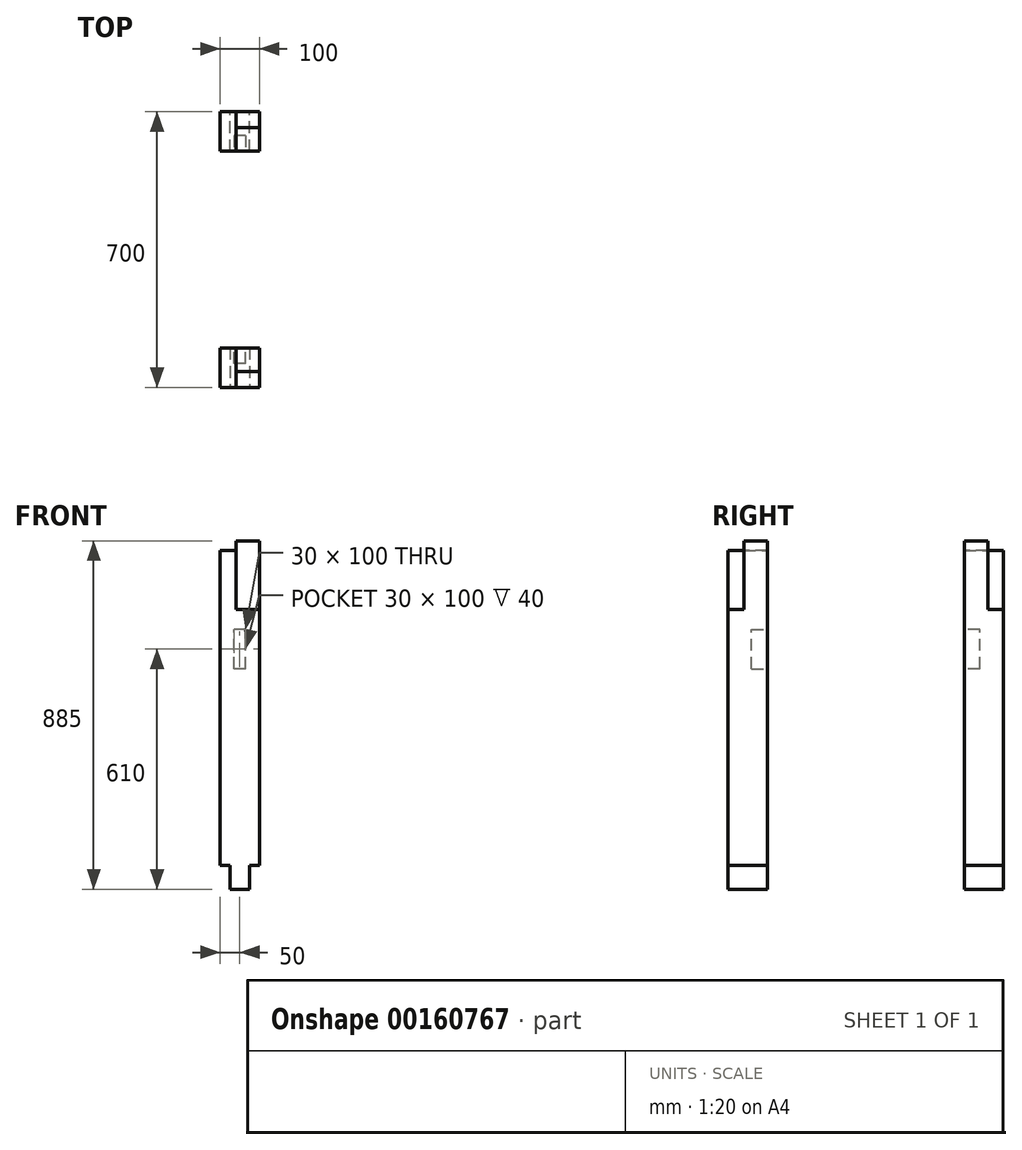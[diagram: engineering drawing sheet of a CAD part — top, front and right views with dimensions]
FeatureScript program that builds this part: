
annotation { "Feature Type Name" : "Feature", "Feature Type Description" : "" }
export const myFeature = defineFeature(function(context is Context, id is Id, definition is map)
    precondition{}
    {
        {
            assignVariable(context, id + "F0", {"name" : "L", "anyValue" : 800 * mm});
        }
        {
            assignVariable(context, id + "F1", {"name" : "t_Feder", "anyValue" : 60 * mm});
        }
        {
            assignVariable(context, id + "F2", {"name" : "t_Tasche", "anyValue" : 40 * mm});
        }
        {
            var Q0;
            Q0=qCreatedBy(makeId("Top.planeOp"),FACE);
            var sketch = newSketch(context, id + "F3", { "sketchPlane" : qUnion([Q0])});
            skLineSegment(sketch, "E0.bottom", {"start": v(50, -50) * mm, "end": v(-50, -50) * mm});
            skLineSegment(sketch, "E0.top", {"start": v(50, 50) * mm, "end": v(-50, 50) * mm});
            skLineSegment(sketch, "E0.left", {"start": v(50, -50) * mm, "end": v(50, 50) * mm});
            skLineSegment(sketch, "E0.right", {"start": v(-50, -50) * mm, "end": v(-50, 50) * mm});
            skPoint(sketch, "E0.middle", {"position": v(0, 0) * mm});
            skSolve(sketch);
        }
        {
            var Q0;
            Q0 = qSketchRegion(id + "F3", true);
            extrude(context, id + "F4", {"entities" : qUnion([Q0]), "depth" : getVariable(context, 'L')});
        }
        {
            var Q0;
            Q0=makeQuery(id+"F4.opExtrude","CAP_FACE",FACE,{"disambiguationData":[OSD([sQuery(id+"F3.wireOp",EDGE,"E0.bottom"),sQuery(id+"F3.wireOp",EDGE,"E0.top"),sQuery(id+"F3.wireOp",EDGE,"E0.left"),sQuery(id+"F3.wireOp",EDGE,"E0.right")])],"isStart":true});
            var sketch = newSketch(context, id + "F5", { "sketchPlane" : qUnion([Q0])});
            skLineSegment(sketch, "E1.bottom", {"start": v(-25, 50) * mm, "end": v(25, 50) * mm});
            skLineSegment(sketch, "E1.top", {"start": v(-25, -50) * mm, "end": v(25, -50) * mm});
            skLineSegment(sketch, "E1.left", {"start": v(-25, 50) * mm, "end": v(-25, -50) * mm});
            skLineSegment(sketch, "E1.right", {"start": v(25, 50) * mm, "end": v(25, -50) * mm});
            skPoint(sketch, "E1.middle", {"position": v(0, 0) * mm});
            skSolve(sketch);
        }
        {
            var Q0;
            Q0 = qSketchRegion(id + "F5", true);
            extrude(context, id + "F6", {"entities" : qUnion([Q0]), "operationType" : NewBodyOperationType.ADD, "depth" : getVariable(context, 't_Feder')});
        }
        {
            var Q0;
            Q0=makeQuery(id+"F6.boolean.opBoolean","MERGE",FACE,{"derivedFrom":[makeQuery(id+"F4.opExtrude","SWEPT_FACE",FACE,{"disambiguationData":[OSD([sQuery(id+"F3.wireOp",EDGE,"E0.bottom")])]}),makeQuery(id+"F6.opExtrude","SWEPT_FACE",FACE,{"disambiguationData":[OSD([sQuery(id+"F5.wireOp",EDGE,"E1.bottom")])]})]});
            var sketch = newSketch(context, id + "F7", { "sketchPlane" : qUnion([Q0])});
            skLineSegment(sketch, "E2.bottom", {"start": v(50, 600) * mm, "end": v(-50, 600) * mm, "construction": true});
            skLineSegment(sketch, "E2.top", {"start": v(50, 500) * mm, "end": v(-50, 500) * mm, "construction": true});
            skLineSegment(sketch, "E2.left", {"start": v(50, 600) * mm, "end": v(50, 500) * mm, "construction": true});
            skLineSegment(sketch, "E2.right", {"start": v(-50, 600) * mm, "end": v(-50, 500) * mm, "construction": true});
            skPoint(sketch, "E2.middle", {"position": v(0, 550) * mm});
            skLineSegment(sketch, "E3", {"start": v(0, 800) * mm, "end": v(0, 550) * mm, "construction": true});
            skLineSegment(sketch, "E4.bottom", {"start": v(15, 500) * mm, "end": v(-15, 500) * mm});
            skLineSegment(sketch, "E4.top", {"start": v(15, 600) * mm, "end": v(-15, 600) * mm});
            skLineSegment(sketch, "E4.left", {"start": v(15, 500) * mm, "end": v(15, 600) * mm});
            skLineSegment(sketch, "E4.right", {"start": v(-15, 500) * mm, "end": v(-15, 600) * mm});
            skSolve(sketch);
        }
        {
            var Q0;
            Q0 = qSketchRegion(id + "F7", true);
            extrude(context, id + "F8", {"entities" : qUnion([Q0]), "operationType" : NewBodyOperationType.REMOVE, "oppositeDirection" : true, "depth" : getVariable(context, 't_Tasche')});
        }
        {
            var Q0;
            Q0=makeQuery(id+"F6.boolean.opBoolean","MERGE",FACE,{"derivedFrom":[makeQuery(id+"F4.opExtrude","SWEPT_FACE",FACE,{"disambiguationData":[OSD([sQuery(id+"F3.wireOp",EDGE,"E0.top")])]}),makeQuery(id+"F6.opExtrude","SWEPT_FACE",FACE,{"disambiguationData":[OSD([sQuery(id+"F5.wireOp",EDGE,"E1.top")])]})]});
            var sketch = newSketch(context, id + "F9", { "sketchPlane" : qUnion([Q0])});
            skLineSegment(sketch, "E5.bottom", {"start": v(-50, 800) * mm, "end": v(10, 800) * mm});
            skLineSegment(sketch, "E5.top", {"start": v(-50, 650) * mm, "end": v(10, 650) * mm});
            skLineSegment(sketch, "E5.left", {"start": v(-50, 800) * mm, "end": v(-50, 650) * mm});
            skLineSegment(sketch, "E5.right", {"start": v(10, 800) * mm, "end": v(10, 650) * mm});
            skPoint(sketch, "E6.orphan", {"position": v(50, 650) * mm});
            skSolve(sketch);
        }
        {
            var Q0;
            Q0 = qSketchRegion(id + "F9", true);
            extrude(context, id + "F10", {"entities" : qUnion([Q0]), "operationType" : NewBodyOperationType.REMOVE, "oppositeDirection" : true, "depth" : 40 * mm});
        }
        {
            var Q0;
            Q0=makeQuery(id+"F4.opExtrude","CAP_FACE",FACE,{"disambiguationData":[OSD([sQuery(id+"F3.wireOp",EDGE,"E0.bottom"),sQuery(id+"F3.wireOp",EDGE,"E0.top"),sQuery(id+"F3.wireOp",EDGE,"E0.left"),sQuery(id+"F3.wireOp",EDGE,"E0.right")])],"isStart":false});
            var sketch = newSketch(context, id + "F11", { "sketchPlane" : qUnion([Q0])});
            skLineSegment(sketch, "E7.bottom", {"start": v(-10, 10) * mm, "end": v(50, 10) * mm});
            skLineSegment(sketch, "E7.top", {"start": v(-10, -50) * mm, "end": v(50, -50) * mm});
            skLineSegment(sketch, "E7.left", {"start": v(-10, 10) * mm, "end": v(-10, -50) * mm});
            skLineSegment(sketch, "E7.right", {"start": v(50, 10) * mm, "end": v(50, -50) * mm});
            skSolve(sketch);
        }
        {
            var Q0;
            Q0 = qSketchRegion(id + "F11", true);
            extrude(context, id + "F12", {"entities" : qUnion([Q0]), "operationType" : NewBodyOperationType.ADD, "depth" : 25 * mm});
        }
        {
            var Q0;
            Q0=qCreatedBy(makeId("Front.planeOp"),FACE);
            cPlane(context, id + "F13", {"entities" : qUnion([Q0]), "cplaneType" : CPlaneType.OFFSET, "offset" : 300 * mm, "width" : 150 * mm, "height" : 150 * mm});
        }
        {
            var Q0;
            Q0=makeQuery(id+"F4.opExtrude","SWEPT_BODY",BODY,{"disambiguationData":[OSD([sQuery(id+"F3.wireOp",EDGE,"E0.bottom"),sQuery(id+"F3.wireOp",EDGE,"E0.top"),sQuery(id+"F3.wireOp",EDGE,"E0.left"),sQuery(id+"F3.wireOp",EDGE,"E0.right")])]});
            var Q1;
            Q1=qCreatedBy(id+"F13.planeOp",FACE);
            mirror(context, id + "F14", {"entities" : qUnion([Q0]), "mirrorPlane" : qUnion([Q1])});
        }
    });
